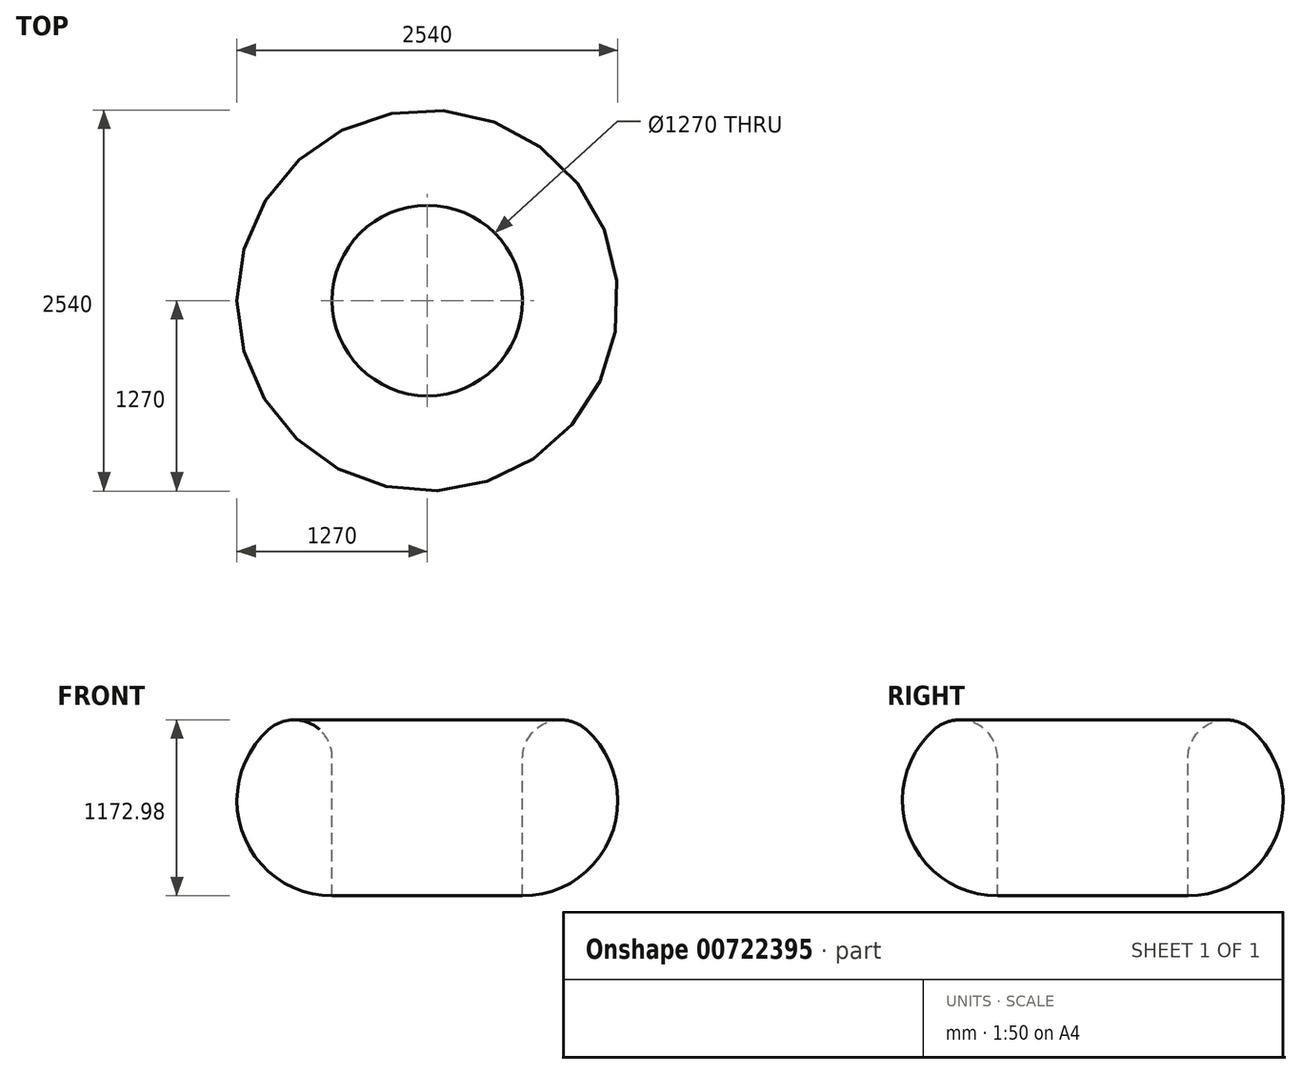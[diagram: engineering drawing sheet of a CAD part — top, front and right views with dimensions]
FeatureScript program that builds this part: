
annotation { "Feature Type Name" : "Feature", "Feature Type Description" : "" }
export const myFeature = defineFeature(function(context is Context, id is Id, definition is map)
    precondition{}
    {
        {
            var Q0;
            Q0=qCreatedBy(makeId("Front.planeOp"),FACE);
            var sketch = newSketch(context, id + "F0", { "sketchPlane" : qUnion([Q0])});
            skLineSegment(sketch, "E0", {"start": v(0, 0) * mm, "end": v(0, 1270) * mm});
            skLineSegment(sketch, "E1", {"start": v(0, 1270) * mm, "end": v(-1270, 1270) * mm});
            skLineSegment(sketch, "E2", {"start": v(-1270, 1270) * mm, "end": v(-1270, 0) * mm});
            skLineSegment(sketch, "E3", {"start": v(-1270, 0) * mm, "end": v(0, 0) * mm});
            skSolve(sketch);
        }
        {
            var Q0;
            Q0=makeQuery(id+"F0.imprint","IMPRINT",FACE,{"disambiguationData":[TD([[makeQuery(id+"F0.imprint","IMPRINT",EDGE,{"derivedFrom":sQuery(id+"F0.wireOp",EDGE,"E0")}),1.0]])]});
            var Q1;
            Q1=sQuery(id+"F0.wireOp",EDGE,"E0");
            revolve(context, id + "F1", {"surfaceOperationType" : NewSurfaceOperationType.NEW, "entities" : qUnion([Q0]), "axis" : qUnion([Q1]), "revolveType" : RevolveType.FULL});
        }
        {
            var Q0;
            Q0=makeQuery(id+"F1.opRevolve","SWEPT_EDGE",EDGE,{"disambiguationData":[OSD([sQuery(id+"F0.wireOp",EDGE,"E1"),sQuery(id+"F0.wireOp",EDGE,"E2")])]});
            var Q1;
            Q1=makeQuery(id+"F1.opRevolve","SWEPT_FACE",FACE,{"disambiguationData":[OSD([sQuery(id+"F0.wireOp",EDGE,"E2")])]});
            fillet(context, id + "F2", {"entities" : qUnion([Q0, Q1]), "radius" : 635 * mm, "tangentPropagation" : true, "allowEdgeOverflow" : false});
        }
        {
            var Q0;
            Q0=makeQuery(id+"F1.opRevolve","SWEPT_FACE",FACE,{"disambiguationData":[OSD([sQuery(id+"F0.wireOp",EDGE,"E1")])]});
            extrude(context, id + "F3", {"entities" : qUnion([Q0]), "operationType" : NewBodyOperationType.REMOVE, "endBound" : BoundingType.THROUGH_ALL, "oppositeDirection" : true, "depth" : 25.4 * mm, "offsetDistance" : 25.4 * mm});
        }
        {
            var Q0;
            {var subQ0=sQuery(id+"F0.wireOp",EDGE,"E2");var subQ1=sQuery(id+"F0.wireOp",EDGE,"E1");Q0=makeQuery(id+"F3.boolean.opBoolean","MERGE",EDGE,{"derivedFrom":[makeQuery(id+"F2.opFillet","BLEND_EDGE",EDGE,{"blendedFrom":[makeQuery(id+"F1.opRevolve","SWEPT_EDGE",EDGE,{"disambiguationData":[OSD([subQ1,subQ0])]}),makeQuery(id+"F1.opRevolve","SWEPT_FACE",FACE,{"disambiguationData":[OSD([subQ1])]})],"blendedInto":[makeQuery(id+"F1.opRevolve","SWEPT_FACE",FACE,{"disambiguationData":[OSD([subQ1])]})]}),makeQuery(id+"F3.opExtrude","CAP_EDGE",EDGE,{"disambiguationData":[OSD([subQ1,subQ0])],"isStart":true})]});}
            var Q1;
            {var subQ0=sQuery(id+"F0.wireOp",EDGE,"E3");Q1=makeQuery(id+"F2.opFillet","BLEND_EDGE",EDGE,{"blendedFrom":[makeQuery(id+"F1.opRevolve","SWEPT_EDGE",EDGE,{"disambiguationData":[OSD([sQuery(id+"F0.wireOp",EDGE,"E2"),subQ0])]}),makeQuery(id+"F1.opRevolve","SWEPT_FACE",FACE,{"disambiguationData":[OSD([subQ0])]})],"blendedInto":[makeQuery(id+"F1.opRevolve","SWEPT_FACE",FACE,{"disambiguationData":[OSD([subQ0])]})]});}
            fillet(context, id + "F4", {"entities" : qUnion([Q0, Q1]), "radius" : 254 * mm, "tangentPropagation" : true, "allowEdgeOverflow" : false});
        }
    });
